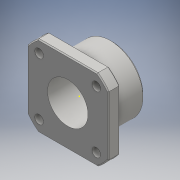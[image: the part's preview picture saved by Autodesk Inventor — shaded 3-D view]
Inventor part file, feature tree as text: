
AUTODESK INVENTOR PART (.ipt)
format: ipt  version: 2016 (Build 200138000, 138)  size: 179,712 bytes
history: native  units: mm
features: sketch x6, extrude x5, chamfer x3
ambient origin geometry x8: Origin, YZ Plane, XZ Plane, XY Plane, X Axis, Y Axis, Z Axis, Center Point
bodies: Solid1 (feature_tree)
feature tree (14):
  extrude  "Extrusion1"  Depth=42.0mm
  extrude  "Extrusion2"  Depth=33.9mm
  extrude  "Extrusion3"  Depth=21.0mm
  sketch  "Sketch4"  dims[d11=76.65mm d12=0.0mm d13=6.5mm]
  extrude  "Extrusion4"  Depth=6.5mm
  chamfer  "Chamfer1"  Distance=40.0mm Angle=360.0deg
  chamfer  "Chamfer2"  Distance=88.15mm
  extrude  "Extrusion5"  Depth=1.0mm TaperAngle=45.0deg
  chamfer  "Chamfer3"  Distance=0.5mm Angle=45.0deg
  sketch  "Sketch1"  dims[d3=42.0mm d4=42.0mm]
  sketch  "Sketch2"  dims[d5=6.0mm d6=0.0mm d7=33.9mm]
  sketch  "Sketch3"  dims[d8=17.1mm d9=0.0mm d10=21.0mm]
  sketch  "Sketch5"  dims[d14=8.0mm]
  sketch  "Sketch6"  dims[d15=4.5mm d16=40.0mm d18=360.0deg d20=88.15mm d21=0.0mm d22=1.0mm d23=2.0mm d24=45.0deg d25=0.5mm d26=2.0mm d27=45.0deg d28=15.5mm d29=219.6mm d30=0.0mm d31=0.5mm d32=2.0mm d33=45.0deg]
